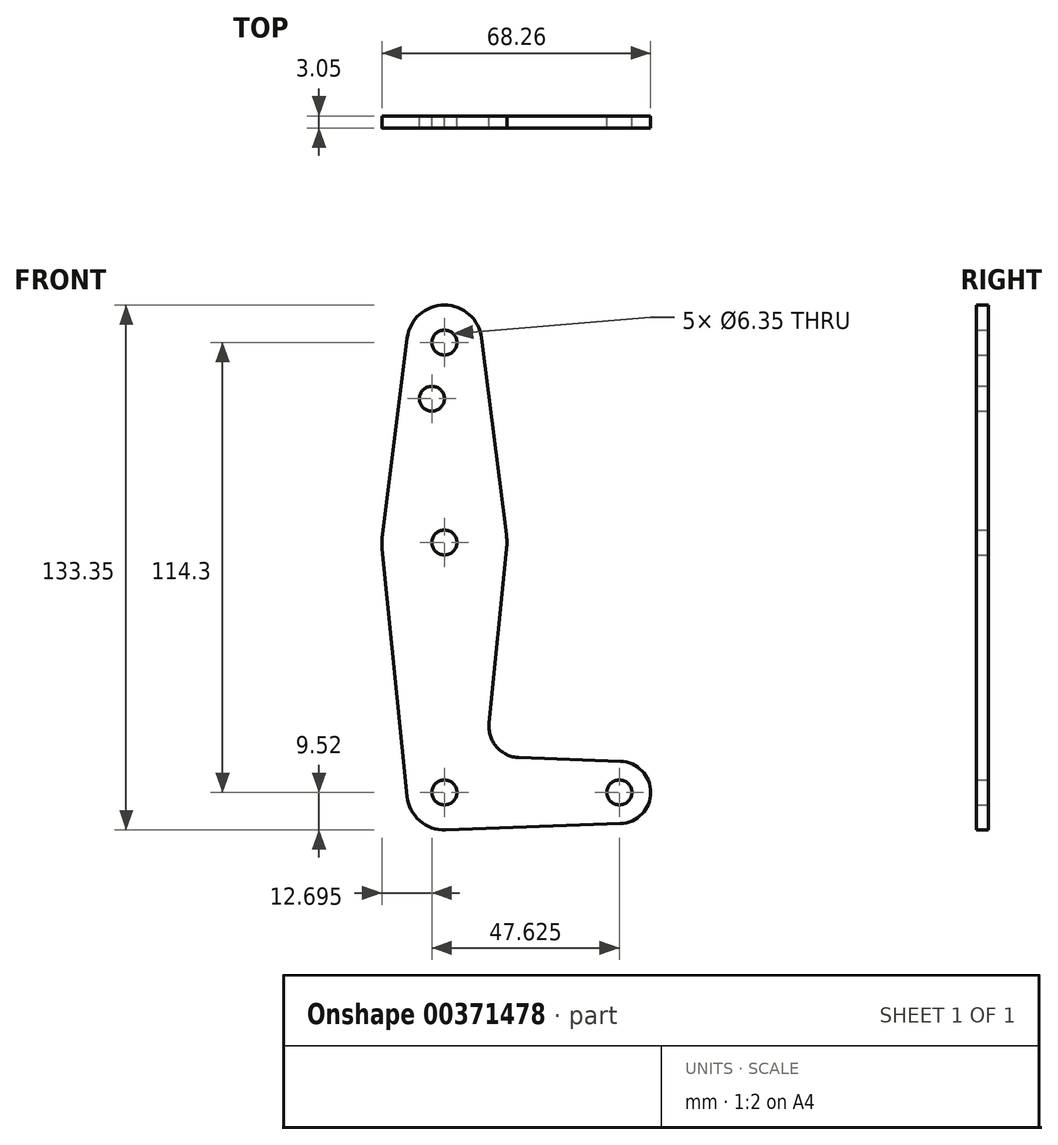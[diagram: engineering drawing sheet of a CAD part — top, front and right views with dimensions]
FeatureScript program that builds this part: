
annotation { "Feature Type Name" : "Feature", "Feature Type Description" : "" }
export const myFeature = defineFeature(function(context is Context, id is Id, definition is map)
    precondition{}
    {
        {
            var Q0;
            Q0=qCreatedBy(makeId("Front.planeOp"),FACE);
            var sketch = newSketch(context, id + "F0", { "sketchPlane" : qUnion([Q0])});
            skCircle(sketch, "E0", {"center": v(0, 0) * mm, "radius": 9.53 * mm});
            skCircle(sketch, "E1", {"center": v(0, 63.5) * mm, "radius": 15.88 * mm});
            skCircle(sketch, "E2", {"center": v(0, 114.3) * mm, "radius": 9.53 * mm});
            skCircle(sketch, "E3", {"center": v(44.45, 0) * mm, "radius": 7.94 * mm});
            skLineSegment(sketch, "E4", {"start": v(0, 114.3) * mm, "end": v(0, 0) * mm, "construction": true});
            skLineSegment(sketch, "E5", {"start": v(44.45, 0) * mm, "end": v(0, 0) * mm, "construction": true});
            skLineSegment(sketch, "E6", {"start": v(-9.45, 115.5) * mm, "end": v(-15.75, 65.48) * mm});
            skLineSegment(sketch, "E7", {"start": v(-15.8, 61.91) * mm, "end": v(-9.48, -0.95) * mm});
            skLineSegment(sketch, "E8", {"start": v(9.45, 115.5) * mm, "end": v(15.75, 65.48) * mm});
            skLineSegment(sketch, "E9", {"start": v(15.8, 61.91) * mm, "end": v(11.34, 17.6) * mm});
            skLineSegment(sketch, "E10", {"start": v(0.34, -9.52) * mm, "end": v(44.73, -7.93) * mm});
            skLineSegment(sketch, "E11", {"start": v(44.73, 7.93) * mm, "end": v(18.97, 8.85) * mm});
            skCircle(sketch, "E12", {"center": v(0, 0) * mm, "radius": 3.18 * mm});
            skCircle(sketch, "E13", {"center": v(0, 114.3) * mm, "radius": 3.18 * mm});
            skCircle(sketch, "E14", {"center": v(0, 63.5) * mm, "radius": 3.18 * mm});
            skCircle(sketch, "E15", {"center": v(44.45, 0) * mm, "radius": 3.18 * mm});
            skCircle(sketch, "E16", {"center": v(-3.17, 100.03) * mm, "radius": 3.18 * mm});
            skArc(sketch, "E17.filletArc", {"start": v(11.34, 17.6) * mm, "mid": v(13.26, 11.57) * mm, "end": v(18.97, 8.85) * mm});
            skSolve(sketch);
        }
        {
            var Q0;
            Q0 = qSketchRegion(id + "F0", true);
            extrude(context, id + "F1", {"entities" : qUnion([Q0]), "depth" : 3.05 * mm});
        }
    });
